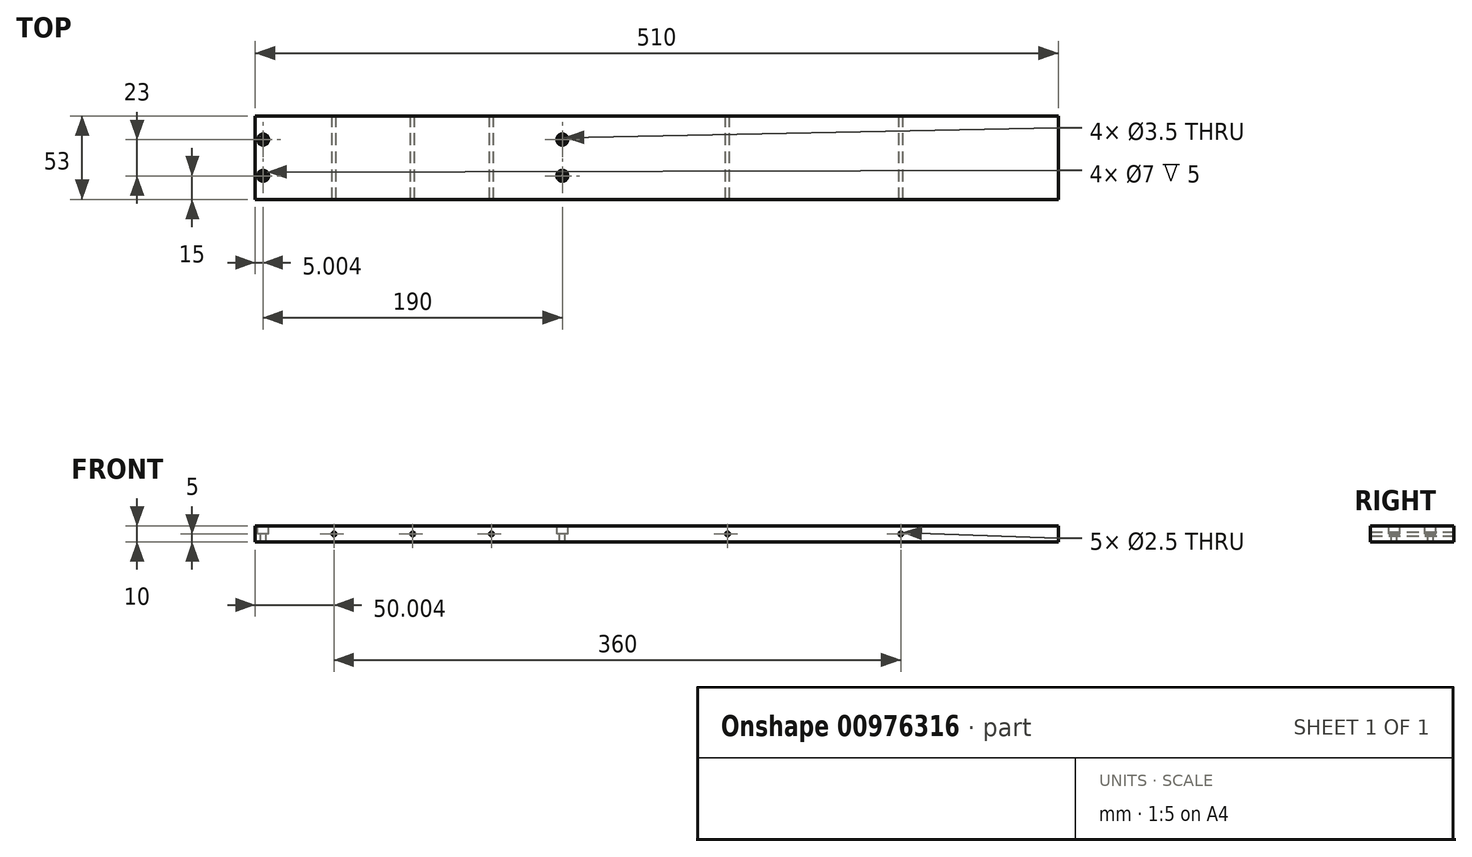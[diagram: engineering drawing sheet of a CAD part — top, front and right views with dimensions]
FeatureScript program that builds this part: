
annotation { "Feature Type Name" : "Feature", "Feature Type Description" : "" }
export const myFeature = defineFeature(function(context is Context, id is Id, definition is map)
    precondition{}
    {
        {
            var Q0;
            Q0=qCreatedBy(makeId("Top.planeOp"),FACE);
            var sketch = newSketch(context, id + "F0", { "sketchPlane" : qUnion([Q0])});
            skLineSegment(sketch, "E0.bottom", {"start": v(-229.19, -6.8) * mm, "end": v(280.81, -6.8) * mm});
            skLineSegment(sketch, "E0.top", {"start": v(-229.19, -59.8) * mm, "end": v(280.81, -59.8) * mm});
            skLineSegment(sketch, "E0.left", {"start": v(-229.19, -6.8) * mm, "end": v(-229.19, -59.8) * mm});
            skLineSegment(sketch, "E0.right", {"start": v(280.81, -6.8) * mm, "end": v(280.81, -59.8) * mm});
            skLineSegment(sketch, "E1", {"start": v(-219.19, -59.8) * mm, "end": v(-219.19, -6.8) * mm});
            skLineSegment(sketch, "E2", {"start": v(-39.19, -6.8) * mm, "end": v(-39.19, -59.8) * mm});
            skLineSegment(sketch, "E3", {"start": v(-29.19, -59.8) * mm, "end": v(-29.19, -6.8) * mm});
            skSolve(sketch);
        }
        {
            var Q0;
            Q0=makeQuery(id+"F0.imprint","IMPRINT",FACE,{"disambiguationData":[TD([[makeQuery(id+"F0.imprint","IMPRINT",EDGE,{"derivedFrom":sQuery(id+"F0.wireOp",EDGE,"E0.bottom")}),-1.0]])]});
            var Q1;
            {var subQ0=sQuery(id+"F0.wireOp",EDGE,"L28E7XbG-5iz7-ZeGE-Me9n-sPyiY5gFP8X4");Q1=makeQuery(id+"F0.imprint","IMPRINT",FACE,{"disambiguationData":[TD([[makeQuery(id+"F0.imprint","IMPRINT",EDGE,{"derivedFrom":subQ0}),1.0]])]});}
            extrude(context, id + "F1", {"entities" : qUnion([Q0, Q1]), "depth" : 10 * mm, "offsetDistance" : 25 * mm});
        }
        {
            var Q0;
            Q0=makeQuery(id+"F1.opExtrude","CAP_FACE",FACE,{"disambiguationData":[OSD([sQuery(id+"F0.wireOp",EDGE,"E0.bottom"),sQuery(id+"F0.wireOp",EDGE,"E0.top"),sQuery(id+"F0.wireOp",EDGE,"E0.left"),sQuery(id+"F0.wireOp",EDGE,"E0.right"),sQuery(id+"F0.wireOp",EDGE,"L28E7XbG-5iz7-ZeGE-Me9n-sPyiY5gFP8X4"),sQuery(id+"F0.wireOp",EDGE,"UREt9wRr-ooZ6-HdO8-bFKl-oGqbFOtlArNg"),sQuery(id+"F0.wireOp",EDGE,"EBIZHZwG-Zgoi-PfuT-vxo1-CHU8m1LLZZ0L")])],"isStart":false});
            var sketch = newSketch(context, id + "F2", { "sketchPlane" : qUnion([Q0])});
            skCircle(sketch, "E4", {"center": v(-224.19, -21.8) * mm, "radius": 2.5 * mm});
            skCircle(sketch, "E5", {"center": v(-224.19, -44.8) * mm, "radius": 2.5 * mm});
            skCircle(sketch, "E6", {"center": v(-34.19, -21.8) * mm, "radius": 2.5 * mm});
            skCircle(sketch, "E7", {"center": v(-34.19, -44.8) * mm, "radius": 2.5 * mm});
            skSolve(sketch);
        }
        {
            var Q0;
            Q0=sQuery(id+"F2.wireOp",VERTEX,"E4.center");
            var Q1;
            Q1=sQuery(id+"F2.wireOp",VERTEX,"E5.center");
            var Q2;
            Q2=sQuery(id+"F2.wireOp",VERTEX,"E6.center");
            var Q3;
            Q3=sQuery(id+"F2.wireOp",VERTEX,"E7.center");
            var Q4;
            Q4=makeQuery(id+"F1.opExtrude","SWEPT_BODY",BODY,{"disambiguationData":[OSD([sQuery(id+"F0.wireOp",EDGE,"E0.bottom"),sQuery(id+"F0.wireOp",EDGE,"E0.top"),sQuery(id+"F0.wireOp",EDGE,"E0.left"),sQuery(id+"F0.wireOp",EDGE,"E0.right"),sQuery(id+"F0.wireOp",EDGE,"L28E7XbG-5iz7-ZeGE-Me9n-sPyiY5gFP8X4"),sQuery(id+"F0.wireOp",EDGE,"UREt9wRr-ooZ6-HdO8-bFKl-oGqbFOtlArNg"),sQuery(id+"F0.wireOp",EDGE,"EBIZHZwG-Zgoi-PfuT-vxo1-CHU8m1LLZZ0L")])]});
            hole(context, id + "F3", {"style" : HoleStyle.C_BORE, "endStyle" : HoleEndStyle.THROUGH, "holeDiameter" : 3.5 * mm, "cBoreDiameter" : 7 * mm, "cBoreDepth" : 5 * mm, "majorDiameter" : 4 * mm, "isTappedThrough" : true, "tappedDepth" : 19.25 * mm, "tapClearance" : 3, "locations" : qUnion([Q0, Q1, Q2, Q3]), "scope" : qUnion([Q4])});
        }
        {
            var Q0;
            Q0=makeQuery(id+"F1.opExtrude","SWEPT_FACE",FACE,{"disambiguationData":[OSD([sQuery(id+"F0.wireOp",EDGE,"E0.bottom")])]});
            var sketch = newSketch(context, id + "F4", { "sketchPlane" : qUnion([Q0])});
            skLineSegment(sketch, "E8", {"start": v(29.19, 10) * mm, "end": v(29.19, 0) * mm});
            skCircle(sketch, "E9", {"center": v(79.19, 5) * mm, "radius": 1.25 * mm});
            skCircle(sketch, "E10", {"center": v(129.19, 5) * mm, "radius": 1.25 * mm});
            skCircle(sketch, "E11", {"center": v(179.19, 5) * mm, "radius": 1.25 * mm});
            skCircle(sketch, "E12", {"center": v(-70.81, 5) * mm, "radius": 1.25 * mm});
            skCircle(sketch, "E13", {"center": v(-180.81, 5) * mm, "radius": 1.25 * mm});
            skSolve(sketch);
        }
        {
            var Q0;
            Q0=makeQuery(id+"F4.imprint","IMPRINT",FACE,{"disambiguationData":[TD([[makeQuery(id+"F4.imprint","IMPRINT",EDGE,{"derivedFrom":sQuery(id+"F4.wireOp",EDGE,"E13")}),1.0]])]});
            var Q1;
            Q1=makeQuery(id+"F4.imprint","IMPRINT",FACE,{"disambiguationData":[TD([[makeQuery(id+"F4.imprint","IMPRINT",EDGE,{"derivedFrom":sQuery(id+"F4.wireOp",EDGE,"E12")}),1.0]])]});
            var Q2;
            Q2=makeQuery(id+"F4.imprint","IMPRINT",FACE,{"disambiguationData":[TD([[makeQuery(id+"F4.imprint","IMPRINT",EDGE,{"derivedFrom":sQuery(id+"F4.wireOp",EDGE,"E9")}),1.0]])]});
            var Q3;
            Q3=makeQuery(id+"F4.imprint","IMPRINT",FACE,{"disambiguationData":[TD([[makeQuery(id+"F4.imprint","IMPRINT",EDGE,{"derivedFrom":sQuery(id+"F4.wireOp",EDGE,"E10")}),1.0]])]});
            var Q4;
            Q4=makeQuery(id+"F4.imprint","IMPRINT",FACE,{"disambiguationData":[TD([[makeQuery(id+"F4.imprint","IMPRINT",EDGE,{"derivedFrom":sQuery(id+"F4.wireOp",EDGE,"E11")}),1.0]])]});
            extrude(context, id + "F5", {"entities" : qUnion([Q0, Q1, Q2, Q3, Q4]), "operationType" : NewBodyOperationType.REMOVE, "endBound" : BoundingType.UP_TO_NEXT, "oppositeDirection" : true, "depth" : 25 * mm, "offsetDistance" : 25 * mm});
        }
    });
